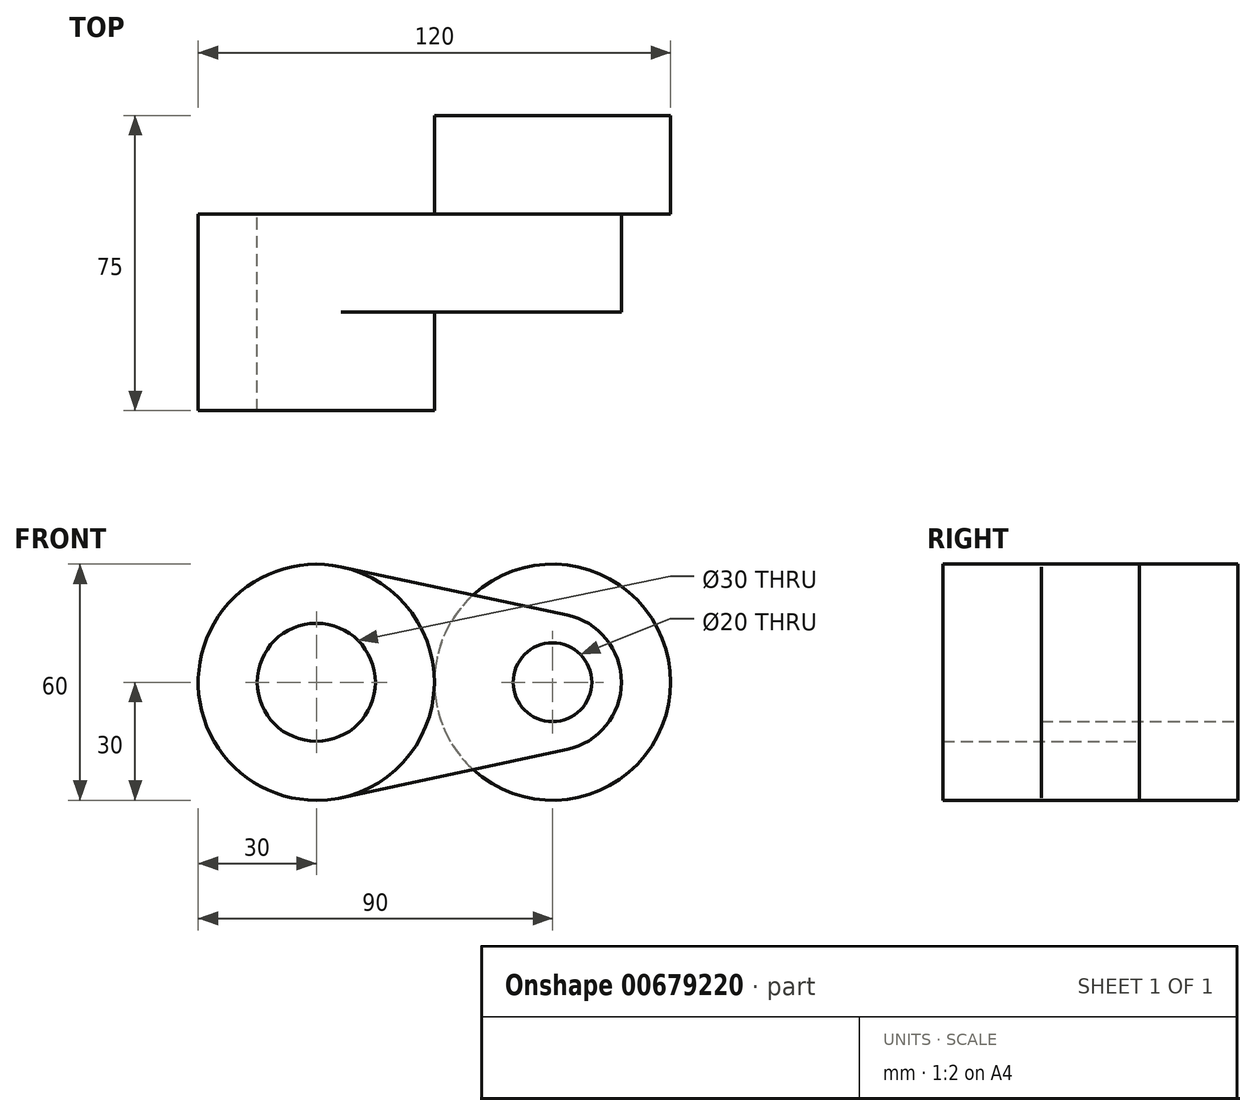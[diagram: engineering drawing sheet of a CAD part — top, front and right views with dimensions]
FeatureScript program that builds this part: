
annotation { "Feature Type Name" : "Feature", "Feature Type Description" : "" }
export const myFeature = defineFeature(function(context is Context, id is Id, definition is map)
    precondition{}
    {
        {
            var Q0;
            Q0=qCreatedBy(makeId("Front.planeOp"),FACE);
            var sketch = newSketch(context, id + "F0", { "sketchPlane" : qUnion([Q0])});
            skCircle(sketch, "E0", {"center": v(0, 0) * mm, "radius": 30 * mm});
            skCircle(sketch, "E1", {"center": v(60, 0) * mm, "radius": 17.5 * mm});
            skLineSegment(sketch, "E2", {"start": v(6.25, 29.34) * mm, "end": v(63.65, 17.12) * mm});
            skLineSegment(sketch, "E3", {"start": v(6.25, -29.34) * mm, "end": v(63.65, -17.12) * mm});
            skCircle(sketch, "E4", {"center": v(0, 0) * mm, "radius": 15 * mm});
            skCircle(sketch, "E5", {"center": v(60, 0) * mm, "radius": 10 * mm});
            skSolve(sketch);
        }
        {
            var Q0;
            Q0=makeQuery(id+"F0.imprint","IMPRINT",FACE,{"disambiguationData":[TD([[makeQuery(id+"F0.imprint","IMPRINT",EDGE,{"derivedFrom":sQuery(id+"F0.wireOp",EDGE,"E4")}),-1.0]])]});
            var Q1;
            {var subQ0=sQuery(id+"F0.wireOp",EDGE,"E2");var subQ1=sQuery(id+"F0.wireOp",EDGE,"E0");var subQ2=makeQuery(id+"F0.imprint","INTERSECT",VERTEX,{"derivedFrom":[subQ1,subQ0]});Q1=makeQuery(id+"F0.imprint","IMPRINT",FACE,{"disambiguationData":[TD([[makeQuery(id+"F0.imprint","IMPRINT",EDGE,{"disambiguationData":[TD([[subQ2,1.0]])],"derivedFrom":subQ1}),-1.0]])]});}
            var Q2;
            {var subQ0=sQuery(id+"F0.wireOp",EDGE,"gNtp6KVH-b1jp-Nyvk-v7Nr-Hhnklb6BGlLA");var subQ1=sQuery(id+"F0.wireOp",EDGE,"E0");var subQ2=makeQuery(id+"F0.imprint","INTERSECT",VERTEX,{"disambiguationData":[OD(0.0)],"derivedFrom":[subQ1,subQ0]});Q2=makeQuery(id+"F0.imprint","IMPRINT",FACE,{"disambiguationData":[TD([[makeQuery(id+"F0.imprint","IMPRINT",EDGE,{"disambiguationData":[TD([[subQ2,1.0]])],"derivedFrom":subQ1}),1.0]])]});}
            var Q3;
            {var subQ3=sQuery(id+"F0.wireOp",EDGE,"gNtp6KVH-b1jp-Nyvk-v7Nr-Hhnklb6BGlLA");var subQ8=sQuery(id+"F0.wireOp",EDGE,"E0");var subQ9=makeQuery(id+"F0.imprint","INTERSECT",VERTEX,{"disambiguationData":[OD(0.0)],"derivedFrom":[subQ8,subQ3]});Q3=makeQuery(id+"F0.imprint","IMPRINT",FACE,{"disambiguationData":[TD([[makeQuery(id+"F0.imprint","IMPRINT",EDGE,{"disambiguationData":[TD([[subQ9,1.0]])],"derivedFrom":subQ8}),-1.0]])]});}
            var Q4;
            {var subQ0=sQuery(id+"F0.wireOp",EDGE,"E3");var subQ1=sQuery(id+"F0.wireOp",EDGE,"E0");var subQ2=makeQuery(id+"F0.imprint","INTERSECT",VERTEX,{"derivedFrom":[subQ1,subQ0]});Q4=makeQuery(id+"F0.imprint","IMPRINT",FACE,{"disambiguationData":[TD([[makeQuery(id+"F0.imprint","IMPRINT",EDGE,{"disambiguationData":[TD([[subQ2,-1.0]])],"derivedFrom":subQ1}),-1.0]])]});}
            var Q5;
            Q5=makeQuery(id+"F0.imprint","IMPRINT",FACE,{"disambiguationData":[TD([[makeQuery(id+"F0.imprint","IMPRINT",EDGE,{"derivedFrom":sQuery(id+"F0.wireOp",EDGE,"E5")}),-1.0]])]});
            extrude(context, id + "F1", {"entities" : qUnion([Q0, Q1, Q2, Q3, Q4, Q5]), "depth" : 25 * mm, "offsetDistance" : 25 * mm});
        }
        {
            var Q0;
            Q0=makeQuery(id+"F0.imprint","IMPRINT",FACE,{"disambiguationData":[TD([[makeQuery(id+"F0.imprint","IMPRINT",EDGE,{"derivedFrom":sQuery(id+"F0.wireOp",EDGE,"E4")}),-1.0]])]});
            var Q1;
            {var subQ0=sQuery(id+"F0.wireOp",EDGE,"gNtp6KVH-b1jp-Nyvk-v7Nr-Hhnklb6BGlLA");var subQ1=sQuery(id+"F0.wireOp",EDGE,"E0");var subQ2=makeQuery(id+"F0.imprint","INTERSECT",VERTEX,{"disambiguationData":[OD(0.0)],"derivedFrom":[subQ1,subQ0]});Q1=makeQuery(id+"F0.imprint","IMPRINT",FACE,{"disambiguationData":[TD([[makeQuery(id+"F0.imprint","IMPRINT",EDGE,{"disambiguationData":[TD([[subQ2,1.0]])],"derivedFrom":subQ1}),1.0]])]});}
            extrude(context, id + "F2", {"entities" : qUnion([Q0, Q1]), "operationType" : NewBodyOperationType.ADD, "depth" : 50 * mm, "offsetDistance" : 25 * mm});
        }
        {
            var Q0;
            Q0=makeQuery(id+"F1.opExtrude","CAP_FACE",FACE,{"disambiguationData":[OSD([sQuery(id+"F0.wireOp",EDGE,"E0"),sQuery(id+"F0.wireOp",EDGE,"E1"),sQuery(id+"F0.wireOp",EDGE,"E2"),sQuery(id+"F0.wireOp",EDGE,"E3"),sQuery(id+"F0.wireOp",EDGE,"E4"),sQuery(id+"F0.wireOp",EDGE,"E5")])],"isStart":true});
            var sketch = newSketch(context, id + "F3", { "sketchPlane" : qUnion([Q0])});
            skCircle(sketch, "E6", {"center": v(-60, 0) * mm, "radius": 30 * mm});
            skCircle(sketch, "E7.0", {"center": v(-60, 0) * mm, "radius": 10 * mm});
            skCircle(sketch, "E8.0", {"center": v(0, 0) * mm, "radius": 30 * mm, "construction": true});
            skSolve(sketch);
        }
        {
            var Q0;
            Q0 = qSketchRegion(id + "F3", true);
            extrude(context, id + "F4", {"entities" : qUnion([Q0]), "operationType" : NewBodyOperationType.ADD, "depth" : 25 * mm, "offsetDistance" : 25 * mm});
        }
    });
